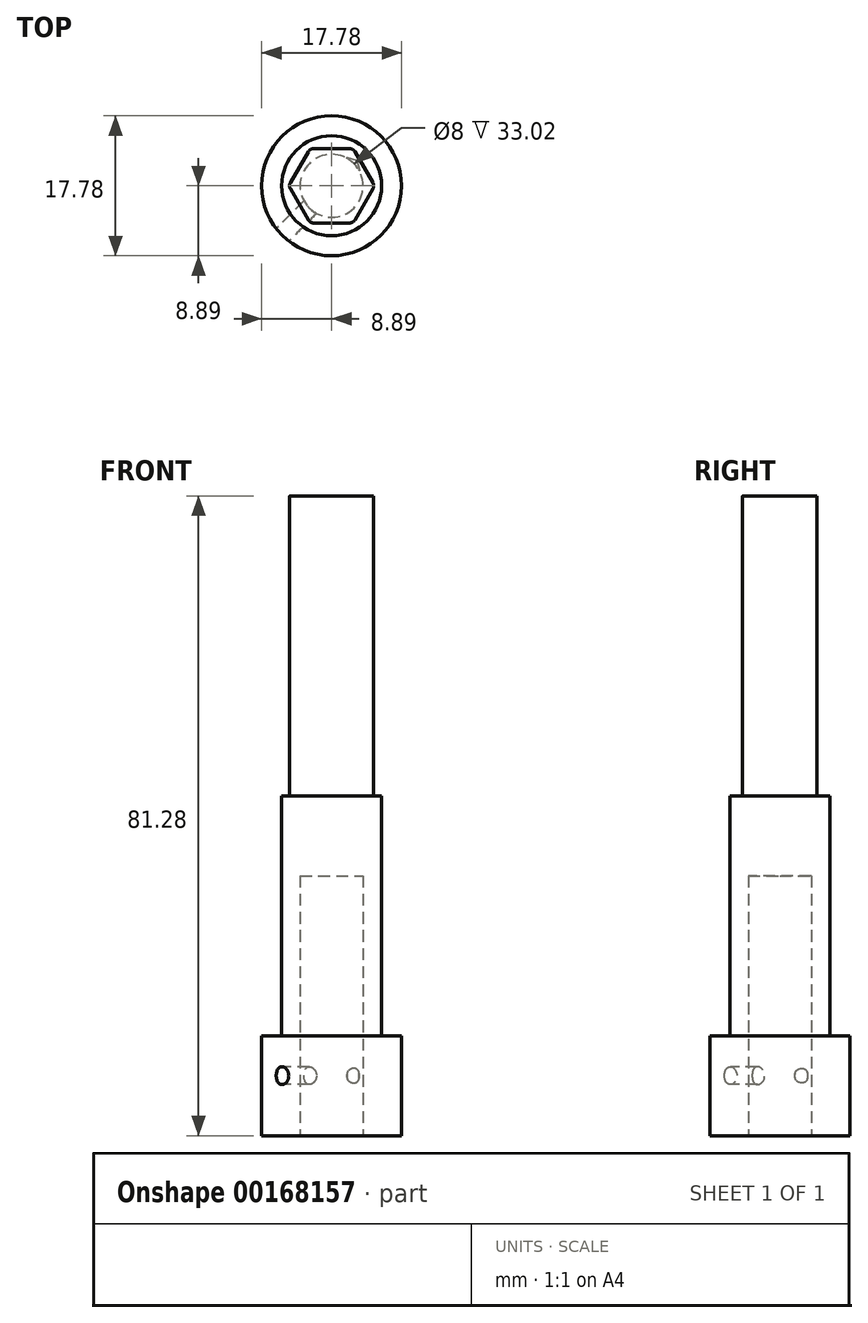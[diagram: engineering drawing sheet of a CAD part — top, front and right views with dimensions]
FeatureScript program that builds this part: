
annotation { "Feature Type Name" : "Feature", "Feature Type Description" : "" }
export const myFeature = defineFeature(function(context is Context, id is Id, definition is map)
    precondition{}
    {
        {
            var Q0;
            Q0=qCreatedBy(makeId("Top.planeOp"),FACE);
            var sketch = newSketch(context, id + "F0", { "sketchPlane" : qUnion([Q0])});
            skCircle(sketch, "E0", {"center": v(0, 0) * mm, "radius": 8.9 * mm});
            skSolve(sketch);
        }
        {
            var Q0;
            Q0=makeQuery(id+"F0.imprint","IMPRINT",FACE,{"disambiguationData":[TD([[makeQuery(id+"F0.imprint","IMPRINT",EDGE,{"derivedFrom":sQuery(id+"F0.wireOp",EDGE,"E0")}),1.0]])]});
            extrude(context, id + "F1", {"entities" : qUnion([Q0]), "depth" : 12.7 * mm});
        }
        {
            var Q0;
            Q0=makeQuery(id+"F1.opExtrude","CAP_FACE",FACE,{"disambiguationData":[OSD([sQuery(id+"F0.wireOp",EDGE,"E0")])],"isStart":false});
            var sketch = newSketch(context, id + "F2", { "sketchPlane" : qUnion([Q0])});
            skCircle(sketch, "E1", {"center": v(0, 0) * mm, "radius": 6.35 * mm});
            skSolve(sketch);
        }
        {
            var Q0;
            Q0=qSketchRegion(id+"F2",true);
            extrude(context, id + "F3", {"entities" : qUnion([Q0]), "operationType" : NewBodyOperationType.ADD, "depth" : 30.48 * mm});
        }
        {
            var Q0;
            Q0=makeQuery(id+"F3.opExtrude","CAP_FACE",FACE,{"disambiguationData":[OSD([sQuery(id+"F2.wireOp",EDGE,"E1")])],"isStart":false});
            var sketch = newSketch(context, id + "F4", { "sketchPlane" : qUnion([Q0])});
            skCircle(sketch, "E2.cCircle", {"center": v(0, 0) * mm, "radius": 4.72 * mm, "construction": true});
            skLineSegment(sketch, "E2.0", {"start": v(5.46, 0) * mm, "end": v(2.73, -4.72) * mm});
            skLineSegment(sketch, "E2.1", {"start": v(2.73, -4.72) * mm, "end": v(-2.73, -4.72) * mm});
            skLineSegment(sketch, "E2.2", {"start": v(-2.73, -4.72) * mm, "end": v(-5.46, 0) * mm});
            skLineSegment(sketch, "E2.3", {"start": v(-5.46, 0) * mm, "end": v(-2.73, 4.72) * mm});
            skLineSegment(sketch, "E2.4", {"start": v(-2.73, 4.72) * mm, "end": v(2.73, 4.72) * mm});
            skLineSegment(sketch, "E2.5", {"start": v(2.73, 4.72) * mm, "end": v(5.46, 0) * mm});
            skPoint(sketch, "E2.0.midPoint", {"position": v(4.1, -2.36) * mm});
            skSolve(sketch);
        }
        {
            var Q0;
            Q0=makeQuery(id+"F4.imprint","IMPRINT",FACE,{"disambiguationData":[TD([[makeQuery(id+"F4.imprint","IMPRINT",EDGE,{"derivedFrom":sQuery(id+"F4.wireOp",EDGE,"E2.0")}),-1.0]])]});
            extrude(context, id + "F5", {"entities" : qUnion([Q0]), "operationType" : NewBodyOperationType.ADD, "depth" : 38.1 * mm});
        }
        {
            var Q0;
            Q0=makeQuery(id+"F5.opExtrude","SWEPT_EDGE",EDGE,{"disambiguationData":[OSD([sQuery(id+"F4.wireOp",EDGE,"E2.1"),sQuery(id+"F4.wireOp",EDGE,"E2.2")])]});
            var Q1;
            Q1=makeQuery(id+"F5.opExtrude","SWEPT_EDGE",EDGE,{"disambiguationData":[OSD([sQuery(id+"F4.wireOp",EDGE,"E2.0"),sQuery(id+"F4.wireOp",EDGE,"E2.1")])]});
            var Q2;
            Q2=makeQuery(id+"F5.opExtrude","SWEPT_EDGE",EDGE,{"disambiguationData":[OSD([sQuery(id+"F4.wireOp",EDGE,"E2.0"),sQuery(id+"F4.wireOp",EDGE,"E2.5")])]});
            var Q3;
            Q3=makeQuery(id+"F5.opExtrude","SWEPT_EDGE",EDGE,{"disambiguationData":[OSD([sQuery(id+"F4.wireOp",EDGE,"E2.4"),sQuery(id+"F4.wireOp",EDGE,"E2.5")])]});
            var Q4;
            Q4=makeQuery(id+"F5.opExtrude","SWEPT_EDGE",EDGE,{"disambiguationData":[OSD([sQuery(id+"F4.wireOp",EDGE,"E2.3"),sQuery(id+"F4.wireOp",EDGE,"E2.4")])]});
            var Q5;
            Q5=makeQuery(id+"F5.opExtrude","SWEPT_EDGE",EDGE,{"disambiguationData":[OSD([sQuery(id+"F4.wireOp",EDGE,"E2.2"),sQuery(id+"F4.wireOp",EDGE,"E2.3")])]});
            fillet(context, id + "F6", {"entities" : qUnion([Q0, Q1, Q2, Q3, Q4, Q5]), "radius" : 0.76 * mm, "tangentPropagation" : true, "allowEdgeOverflow" : false});
        }
        {
            var Q0;
            Q0=makeQuery(id+"F1.opExtrude","CAP_FACE",FACE,{"disambiguationData":[OSD([sQuery(id+"F0.wireOp",EDGE,"E0")])],"isStart":true});
            var sketch = newSketch(context, id + "F7", { "sketchPlane" : qUnion([Q0])});
            skCircle(sketch, "E3", {"center": v(0, 0) * mm, "radius": 4 * mm});
            skSolve(sketch);
        }
        {
            var Q0;
            Q0 = qSketchRegion(id + "F7", true);
            extrude(context, id + "F8", {"entities" : qUnion([Q0]), "operationType" : NewBodyOperationType.REMOVE, "oppositeDirection" : true, "depth" : 33.02 * mm});
        }
        {
            var Q0;
            Q0=qCreatedBy(makeId("Front.planeOp"),FACE);
            var sketch = newSketch(context, id + "F9", { "sketchPlane" : qUnion([Q0])});
            skLineSegment(sketch, "E4", {"start": v(0, 0) * mm, "end": v(0, 37.16) * mm, "construction": true});
            skSolve(sketch);
        }
        {
            var Q0;
            Q0=sQuery(id+"F9.wireOp",EDGE,"E4");
            cPlane(context, id + "F10", {"entities" : qUnion([Q0]), "cplaneType" : CPlaneType.LINE_ANGLE, "offset" : 25.4 * mm, "angle" : 45 * degree, "width" : 152.4 * mm, "height" : 152.4 * mm});
        }
        {
            var Q0;
            Q0=makeQuery(id+"F1.opExtrude","CAP_FACE",FACE,{"disambiguationData":[OSD([sQuery(id+"F0.wireOp",EDGE,"E0")])],"isStart":false});
            var sketch = newSketch(context, id + "F11", { "sketchPlane" : qUnion([Q0])});
            skCircle(sketch, "E5.0", {"center": v(0, 0) * mm, "radius": 8.9 * mm, "construction": true});
            skLineSegment(sketch, "E6", {"start": v(0, 0) * mm, "end": v(-6.29, -6.29) * mm, "construction": true});
            skSolve(sketch);
        }
        {
            var Q0;
            Q0=qCreatedBy(id+"F10.planeOp",FACE);
            var Q1;
            Q1=sQuery(id+"F11.wireOp",VERTEX,"E6.end");
            cPlane(context, id + "F12", {"entities" : qUnion([Q0, Q1]), "cplaneType" : CPlaneType.PLANE_POINT, "offset" : 25.4 * mm, "width" : 152.4 * mm, "height" : 152.4 * mm});
        }
        {
            var Q0;
            Q0=qCreatedBy(id+"F12.planeOp",FACE);
            var sketch = newSketch(context, id + "F13", { "sketchPlane" : qUnion([Q0])});
            skLineSegment(sketch, "E7", {"start": v(0, 12.7) * mm, "end": v(0, 7.62) * mm, "construction": true});
            skPoint(sketch, "E8", {"position": v(0, 7.62) * mm});
            skSolve(sketch);
        }
        {
            var Q0;
            Q0=sQuery(id+"F13.wireOp",VERTEX,"E8");
            var Q1;
            Q1=makeQuery(id+"F1.opExtrude","SWEPT_BODY",BODY,{"disambiguationData":[OSD([sQuery(id+"F0.wireOp",EDGE,"E0")])]});
            hole(context, id + "F14", {"style" : HoleStyle.SIMPLE, "endStyle" : HoleEndStyle.BLIND, "oppositeDirection" : true, "standardTappedOrClearance" : lookupTablePath({ "standard" : "ANSI", "engagement" : "75%", "pitch" : "40 tpi", "size" : "#4", "type" : "Tapped" }), "standardBlindInLast" : lookupTablePath({ "standard" : "ANSI", "engagement" : "75%", "pitch" : "40 tpi", "size" : "#4", "type" : "Tapped" }), "holeDiameter" : 2.26 * mm, "holeDepth" : 12.7 * mm, "locations" : qUnion([Q0]), "scope" : qUnion([Q1]), "majorDiameter" : 2.84 * mm});
        }
    });
